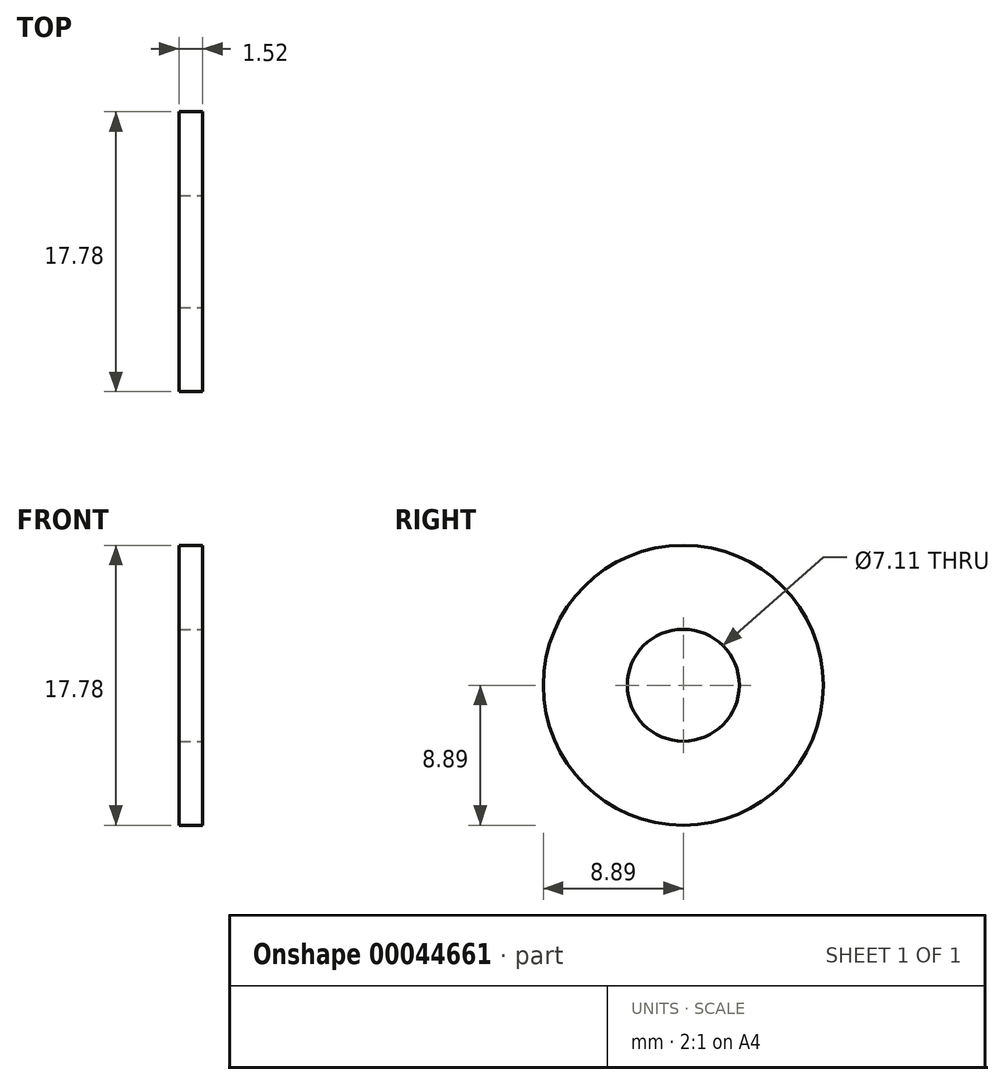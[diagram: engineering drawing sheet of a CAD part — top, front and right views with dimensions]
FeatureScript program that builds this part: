
annotation { "Feature Type Name" : "Feature", "Feature Type Description" : "" }
export const myFeature = defineFeature(function(context is Context, id is Id, definition is map)
    precondition{}
    {
        {
            var Q0;
            Q0=qCreatedBy(makeId("Right.planeOp"),FACE);
            var sketch = newSketch(context, id + "F0", { "sketchPlane" : qUnion([Q0])});
            skCircle(sketch, "E0", {"center": v(0, 0) * mm, "radius": 8.9 * mm});
            skSolve(sketch);
        }
        {
            var Q0;
            Q0=makeQuery(id+"F0.imprint","IMPRINT",FACE,{"disambiguationData":[TD([[makeQuery(id+"F0.imprint","IMPRINT",EDGE,{"derivedFrom":sQuery(id+"F0.wireOp",EDGE,"E0")}),1.0]])]});
            extrude(context, id + "F1", {"entities" : qUnion([Q0]), "depth" : 1.52 * mm});
        }
        {
            var Q0;
            Q0=makeQuery(id+"F1.opExtrude","CAP_FACE",FACE,{"disambiguationData":[OSD([sQuery(id+"F0.wireOp",EDGE,"E0")])],"isStart":false});
            var sketch = newSketch(context, id + "F2", { "sketchPlane" : qUnion([Q0])});
            skPoint(sketch, "E1", {"position": v(0, 0) * mm});
            skSolve(sketch);
        }
        {
            var Q0;
            Q0=sQuery(id+"F2.wireOp",VERTEX,"E1");
            var Q1;
            Q1=makeQuery(id+"F1.opExtrude","SWEPT_BODY",BODY,{"disambiguationData":[OSD([sQuery(id+"F0.wireOp",EDGE,"E0")])]});
            hole(context, id + "F3", {"style" : HoleStyle.SIMPLE, "holeDiameter" : 7.11 * mm, "endStyle" : HoleEndStyle.THROUGH, "locations" : qUnion([Q0]), "scope" : qUnion([Q1])});
        }
    });
